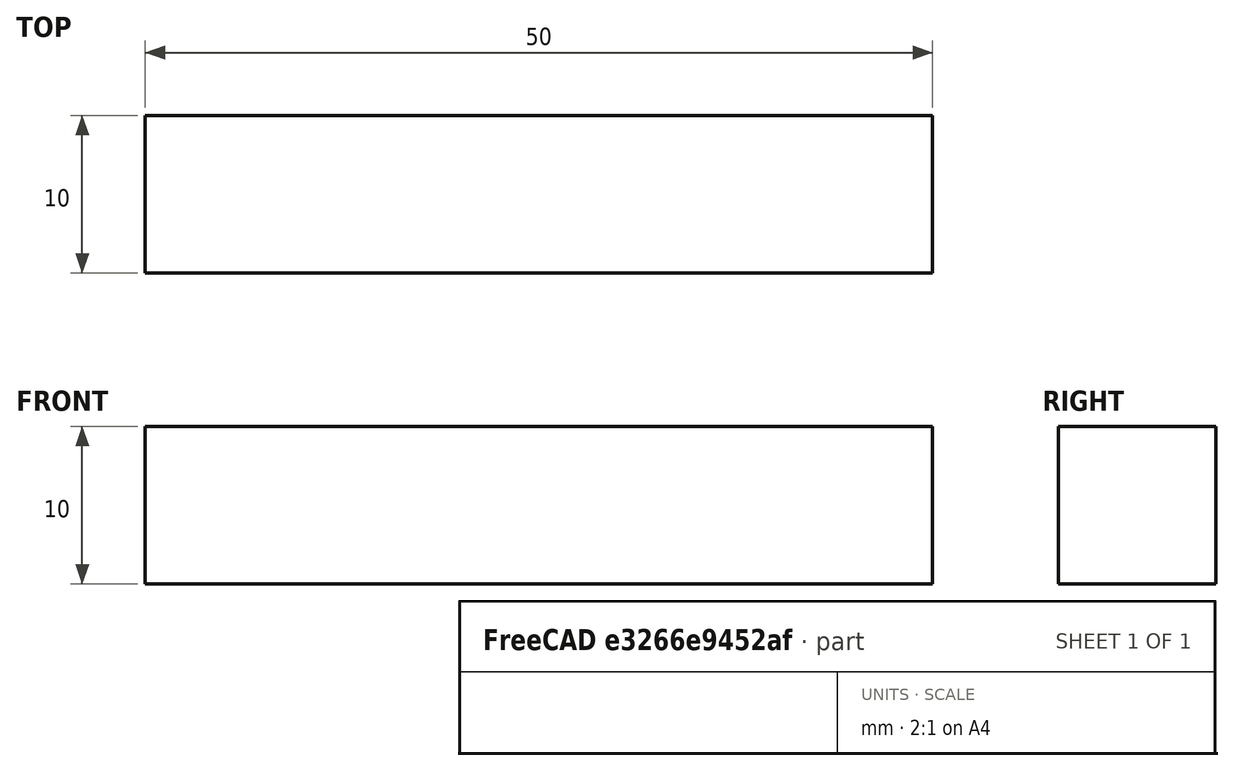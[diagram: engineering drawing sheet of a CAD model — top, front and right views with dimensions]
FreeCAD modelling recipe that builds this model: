
FCSTD DOCUMENT  (FreeCAD 1.0R38641 +678 (Git))
Label: ParametricCube
License: All rights reserved
LicenseURL: https://en.wikipedia.org/wiki/All_rights_reserved
objects: Spreadsheet::Sheet×1, Sketcher::SketchObject×1, PartDesign::Pad×1, PartDesign::Body×1
note: 6 computed .brp shape members not serialized (recipe doc carries the construction recipe); baked Part::Feature solids carry a one-line shape summary decoded from their .brp

FEATURE [Spreadsheet::Sheet] Spreadsheet
  cells = A1='width; B1(width)=50; A2='length; B2(length)=10; A3='height; B3(height)=10
FEATURE [Sketcher::SketchObject] Sketch
  ArcFitTolerance = 1e-06
  AttachmentSupport = -> [XY_Plane]
  FullyConstrained = true
  MakeInternals = false
  MapMode = 5
  expr: Constraints[10] = Spreadsheet.width
  expr: Constraints[9] = Spreadsheet.length
  sketch-geometry (4):
    g0: LineSegment StartX=0 StartY=0 StartZ=0 EndX=50 EndY=0 EndZ=0
    g1: LineSegment StartX=50 StartY=0 StartZ=0 EndX=50 EndY=10 EndZ=0
    g2: LineSegment StartX=50 StartY=10 StartZ=0 EndX=0 EndY=10 EndZ=0
    g3: LineSegment StartX=0 StartY=10 StartZ=0 EndX=0 EndY=0 EndZ=0
  constraints (11):
    c: Coincident(g0,g1)
    c: Coincident(g1,g2)
    c: Coincident(g2,g3)
    c: Coincident(g3,g0)
    c: Horizontal(g0)
    c: Horizontal(g2)
    c: Vertical(g1)
    c: Vertical(g3)
    c: Coincident(g0,g-1)
    c: DistanceY(g1,g1) = 10
    c: DistanceX(g2,g2) = 50
FEATURE [PartDesign::Pad] Pad
  Direction = (0,0,1)
  Length = 10
  Length2 = 10
  Profile = -> Sketch
  ReferenceAxis = -> Sketch [N_Axis]
  Refine = true
  Suppressed = false
  Type = 0
  expr: Length = Spreadsheet.height
FEATURE [PartDesign::Body] Body
  AllowCompound = false
  Group = -> [Sketch,Pad]
  Origin = -> Origin
  Tip = -> Pad
